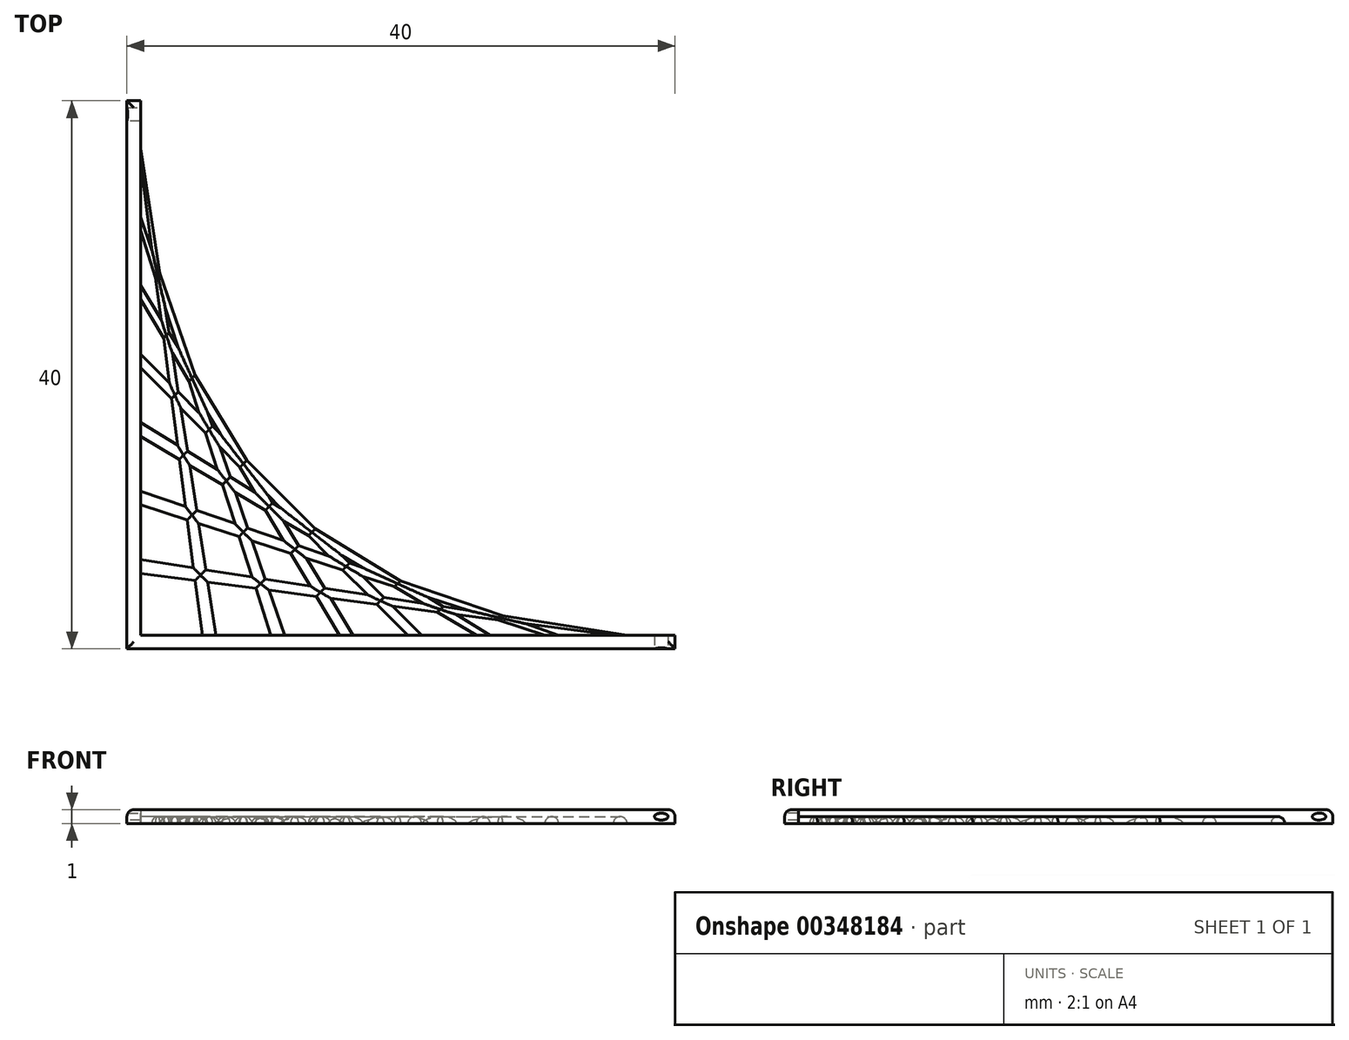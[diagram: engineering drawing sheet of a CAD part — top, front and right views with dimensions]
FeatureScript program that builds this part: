
annotation { "Feature Type Name" : "Feature", "Feature Type Description" : "" }
export const myFeature = defineFeature(function(context is Context, id is Id, definition is map)
    precondition{}
    {
        {
            var Q0;
            Q0=qCreatedBy(makeId("Top.planeOp"),FACE);
            var sketch = newSketch(context, id + "F0", { "sketchPlane" : qUnion([Q0])});
            skLineSegment(sketch, "E0.bottom", {"start": v(0, 0) * mm, "end": v(40, 0) * mm});
            skLineSegment(sketch, "E0.top", {"start": v(0, 1) * mm, "end": v(40, 1) * mm});
            skLineSegment(sketch, "E0.left", {"start": v(0, 0) * mm, "end": v(0, 1) * mm});
            skLineSegment(sketch, "E0.right", {"start": v(40, 0) * mm, "end": v(40, 1) * mm});
            skLineSegment(sketch, "E1.bottom", {"start": v(0, 0) * mm, "end": v(1, 0) * mm});
            skLineSegment(sketch, "E1.top", {"start": v(0, 40) * mm, "end": v(1, 40) * mm});
            skLineSegment(sketch, "E1.left", {"start": v(0, 0) * mm, "end": v(0, 40) * mm});
            skLineSegment(sketch, "E1.right", {"start": v(1, 0) * mm, "end": v(1, 40) * mm});
            skSolve(sketch);
        }
        {
            var Q0;
            Q0 = qSketchRegion(id + "F0", true);
            extrude(context, id + "F1", {"entities" : qUnion([Q0]), "endBound" : BoundingType.SYMMETRIC, "depth" : 1 * mm});
        }
        {
            var Q0;
            Q0=makeQuery(id+"F1.opExtrude","SWEPT_FACE",FACE,{"disambiguationData":[OSD([sQuery(id+"F0.wireOp",EDGE,"E1.right")])]});
            var sketch = newSketch(context, id + "F2", { "sketchPlane" : qUnion([Q0])});
            skArc(sketch, "E2", {"start": v(6.5, -0.5) * mm, "mid": v(6, 0) * mm, "end": v(5.5, -0.5) * mm});
            skLineSegment(sketch, "E3", {"start": v(5.5, -0.5) * mm, "end": v(6.5, -0.5) * mm});
            skArc(sketch, "E4.1.0.0", {"start": v(11.5, -0.5) * mm, "mid": v(11, 0) * mm, "end": v(10.5, -0.5) * mm});
            skArc(sketch, "E4.2.0.0", {"start": v(16.5, -0.5) * mm, "mid": v(16, 0) * mm, "end": v(15.5, -0.5) * mm});
            skArc(sketch, "E4.3.0.0", {"start": v(21.5, -0.5) * mm, "mid": v(21, 0) * mm, "end": v(20.5, -0.5) * mm});
            skArc(sketch, "E4.4.0.0", {"start": v(26.5, -0.5) * mm, "mid": v(26, 0) * mm, "end": v(25.5, -0.5) * mm});
            skLineSegment(sketch, "E4.direction1", {"start": v(5.5, -0.5) * mm, "end": v(10.5, -0.5) * mm, "construction": true});
            skArc(sketch, "E5.0.5.0", {"start": v(31.5, -0.5) * mm, "mid": v(31, 0) * mm, "end": v(30.5, -0.5) * mm});
            skArc(sketch, "E5.0.6.0", {"start": v(36.5, -0.5) * mm, "mid": v(36, 0) * mm, "end": v(35.5, -0.5) * mm});
            skSolve(sketch);
        }
        {
            var Q0;
            Q0=makeQuery(id+"F1.opExtrude","SWEPT_FACE",FACE,{"disambiguationData":[OSD([sQuery(id+"F0.wireOp",EDGE,"E0.top")])]});
            var sketch = newSketch(context, id + "F3", { "sketchPlane" : qUnion([Q0])});
            skArc(sketch, "E6", {"start": v(-5.5, -0.5) * mm, "mid": v(-6, 0) * mm, "end": v(-6.5, -0.5) * mm});
            skLineSegment(sketch, "E7", {"start": v(-5.5, -0.5) * mm, "end": v(-6.5, -0.5) * mm});
            skArc(sketch, "E8.1.0.0", {"start": v(-10.5, -0.5) * mm, "mid": v(-11, 0) * mm, "end": v(-11.5, -0.5) * mm});
            skArc(sketch, "E8.2.0.0", {"start": v(-15.5, -0.5) * mm, "mid": v(-16, 0) * mm, "end": v(-16.5, -0.5) * mm});
            skArc(sketch, "E8.3.0.0", {"start": v(-20.5, -0.5) * mm, "mid": v(-21, 0) * mm, "end": v(-21.5, -0.5) * mm});
            skArc(sketch, "E8.4.0.0", {"start": v(-25.5, -0.5) * mm, "mid": v(-26, 0) * mm, "end": v(-26.5, -0.5) * mm});
            skLineSegment(sketch, "E8.direction1", {"start": v(-6.5, -0.5) * mm, "end": v(-11.5, -0.5) * mm, "construction": true});
            skArc(sketch, "E9.0.5.0", {"start": v(-30.5, -0.5) * mm, "mid": v(-31, 0) * mm, "end": v(-31.5, -0.5) * mm});
            skArc(sketch, "E9.0.6.0", {"start": v(-35.5, -0.5) * mm, "mid": v(-36, 0) * mm, "end": v(-36.5, -0.5) * mm});
            skSolve(sketch);
        }
        {
            var Q1;
            Q1=makeQuery(id+"F2.imprint","IMPRINT",FACE,{"disambiguationData":[TD([[makeQuery(id+"F2.imprint","IMPRINT",EDGE,{"derivedFrom":sQuery(id+"F2.wireOp",EDGE,"E2")}),1.0]])]});
            var Q2;
            {var subQ0=sQuery(id+"F3.wireOp",EDGE,"E9.0.6.0");Q2=makeQuery(id+"F3.imprint","IMPRINT",FACE,{"disambiguationData":[TD([[makeQuery(id+"F3.imprint","IMPRINT",EDGE,{"derivedFrom":subQ0}),1.0]])]});}
            loft(context, id + "F4", {"operationType" : NewBodyOperationType.ADD, "sheetProfilesArray" : [{ "sheetProfileEntities" : qUnion([Q1]) }, { "sheetProfileEntities" : qUnion([Q2]) }]});
        }
        {
            var Q1;
            {var subQ0=sQuery(id+"F2.wireOp",EDGE,"E4.1.0.0");Q1=makeQuery(id+"F2.imprint","IMPRINT",FACE,{"disambiguationData":[TD([[makeQuery(id+"F2.imprint","IMPRINT",EDGE,{"derivedFrom":subQ0}),1.0]])]});}
            var Q2;
            {var subQ0=sQuery(id+"F3.wireOp",EDGE,"E9.0.5.0");Q2=makeQuery(id+"F3.imprint","IMPRINT",FACE,{"disambiguationData":[TD([[makeQuery(id+"F3.imprint","IMPRINT",EDGE,{"derivedFrom":subQ0}),1.0]])]});}
            loft(context, id + "F5", {"operationType" : NewBodyOperationType.ADD, "sheetProfilesArray" : [{ "sheetProfileEntities" : qUnion([Q1]) }, { "sheetProfileEntities" : qUnion([Q2]) }]});
        }
        {
            var Q1;
            {var subQ0=sQuery(id+"F2.wireOp",EDGE,"E4.2.0.0");Q1=makeQuery(id+"F2.imprint","IMPRINT",FACE,{"disambiguationData":[TD([[makeQuery(id+"F2.imprint","IMPRINT",EDGE,{"derivedFrom":subQ0}),1.0]])]});}
            var Q2;
            {var subQ0=sQuery(id+"F3.wireOp",EDGE,"E8.4.0.0");Q2=makeQuery(id+"F3.imprint","IMPRINT",FACE,{"disambiguationData":[TD([[makeQuery(id+"F3.imprint","IMPRINT",EDGE,{"derivedFrom":subQ0}),1.0]])]});}
            loft(context, id + "F6", {"operationType" : NewBodyOperationType.ADD, "sheetProfilesArray" : [{ "sheetProfileEntities" : qUnion([Q1]) }, { "sheetProfileEntities" : qUnion([Q2]) }]});
        }
        {
            var Q1;
            {var subQ0=sQuery(id+"F2.wireOp",EDGE,"E4.3.0.0");Q1=makeQuery(id+"F2.imprint","IMPRINT",FACE,{"disambiguationData":[TD([[makeQuery(id+"F2.imprint","IMPRINT",EDGE,{"derivedFrom":subQ0}),1.0]])]});}
            var Q2;
            {var subQ0=sQuery(id+"F3.wireOp",EDGE,"E8.3.0.0");Q2=makeQuery(id+"F3.imprint","IMPRINT",FACE,{"disambiguationData":[TD([[makeQuery(id+"F3.imprint","IMPRINT",EDGE,{"derivedFrom":subQ0}),1.0]])]});}
            loft(context, id + "F7", {"operationType" : NewBodyOperationType.ADD, "sheetProfilesArray" : [{ "sheetProfileEntities" : qUnion([Q1]) }, { "sheetProfileEntities" : qUnion([Q2]) }]});
        }
        {
            var Q1;
            {var subQ0=sQuery(id+"F2.wireOp",EDGE,"E4.4.0.0");Q1=makeQuery(id+"F2.imprint","IMPRINT",FACE,{"disambiguationData":[TD([[makeQuery(id+"F2.imprint","IMPRINT",EDGE,{"derivedFrom":subQ0}),1.0]])]});}
            var Q2;
            {var subQ0=sQuery(id+"F3.wireOp",EDGE,"E8.2.0.0");Q2=makeQuery(id+"F3.imprint","IMPRINT",FACE,{"disambiguationData":[TD([[makeQuery(id+"F3.imprint","IMPRINT",EDGE,{"derivedFrom":subQ0}),1.0]])]});}
            loft(context, id + "F8", {"operationType" : NewBodyOperationType.ADD, "sheetProfilesArray" : [{ "sheetProfileEntities" : qUnion([Q1]) }, { "sheetProfileEntities" : qUnion([Q2]) }]});
        }
        {
            var Q1;
            {var subQ0=sQuery(id+"F2.wireOp",EDGE,"E5.0.5.0");Q1=makeQuery(id+"F2.imprint","IMPRINT",FACE,{"disambiguationData":[TD([[makeQuery(id+"F2.imprint","IMPRINT",EDGE,{"derivedFrom":subQ0}),1.0]])]});}
            var Q2;
            {var subQ0=sQuery(id+"F3.wireOp",EDGE,"E8.1.0.0");Q2=makeQuery(id+"F3.imprint","IMPRINT",FACE,{"disambiguationData":[TD([[makeQuery(id+"F3.imprint","IMPRINT",EDGE,{"derivedFrom":subQ0}),1.0]])]});}
            loft(context, id + "F9", {"operationType" : NewBodyOperationType.ADD, "sheetProfilesArray" : [{ "sheetProfileEntities" : qUnion([Q1]) }, { "sheetProfileEntities" : qUnion([Q2]) }]});
        }
        {
            var Q1;
            {var subQ0=sQuery(id+"F2.wireOp",EDGE,"E5.0.6.0");Q1=makeQuery(id+"F2.imprint","IMPRINT",FACE,{"disambiguationData":[TD([[makeQuery(id+"F2.imprint","IMPRINT",EDGE,{"derivedFrom":subQ0}),1.0]])]});}
            var Q2;
            Q2=makeQuery(id+"F3.imprint","IMPRINT",FACE,{"disambiguationData":[TD([[makeQuery(id+"F3.imprint","IMPRINT",EDGE,{"derivedFrom":sQuery(id+"F3.wireOp",EDGE,"E6")}),1.0]])]});
            loft(context, id + "F10", {"operationType" : NewBodyOperationType.ADD, "sheetProfilesArray" : [{ "sheetProfileEntities" : qUnion([Q1]) }, { "sheetProfileEntities" : qUnion([Q2]) }]});
        }
        {
            var Q0;
            Q0=makeQuery(id+"F1.opExtrude","SWEPT_FACE",FACE,{"disambiguationData":[OSD([sQuery(id+"F0.wireOp",EDGE,"E1.left")])]});
            var sketch = newSketch(context, id + "F11", { "sketchPlane" : qUnion([Q0])});
            skEllipse(sketch, "E10", {"center": v(-39, 0) * mm, "majorRadius": 0.5 * mm, "minorRadius": 0.25 * mm, "majorAxis": v(1, 0)});
            skSolve(sketch);
        }
        {
            var Q0;
            Q0=makeQuery(id+"F11.imprint","IMPRINT",FACE,{"disambiguationData":[TD([[makeQuery(id+"F11.imprint","IMPRINT",EDGE,{"derivedFrom":sQuery(id+"F11.wireOp",EDGE,"E10")}),1.0]])]});
            var Q1;
            Q1=sQuery(id+"F11.wireOp",EDGE,"E10");
            extrude(context, id + "F12", {"entities" : qUnion([Q0]), "operationType" : NewBodyOperationType.REMOVE, "surfaceEntities" : qUnion([Q1]), "endBound" : BoundingType.THROUGH_ALL, "oppositeDirection" : true, "depth" : 25 * mm});
        }
        {
            var Q0;
            Q0=makeQuery(id+"F1.opExtrude","SWEPT_FACE",FACE,{"disambiguationData":[OSD([sQuery(id+"F0.wireOp",EDGE,"E0.bottom"),sQuery(id+"F0.wireOp",EDGE,"E1.bottom")])]});
            var sketch = newSketch(context, id + "F13", { "sketchPlane" : qUnion([Q0])});
            skEllipse(sketch, "E11", {"center": v(39, 0) * mm, "majorRadius": 0.5 * mm, "minorRadius": 0.25 * mm, "majorAxis": v(1, 0)});
            skSolve(sketch);
        }
        {
            var Q0;
            Q0=makeQuery(id+"F13.imprint","IMPRINT",FACE,{"disambiguationData":[TD([[makeQuery(id+"F13.imprint","IMPRINT",EDGE,{"derivedFrom":sQuery(id+"F13.wireOp",EDGE,"E11")}),1.0]])]});
            extrude(context, id + "F14", {"entities" : qUnion([Q0]), "operationType" : NewBodyOperationType.REMOVE, "endBound" : BoundingType.THROUGH_ALL, "oppositeDirection" : true, "depth" : 25 * mm});
        }
        {
            var Q0;
            Q0=makeQuery(id+"F1.opExtrude","CAP_EDGE",EDGE,{"disambiguationData":[OSD([sQuery(id+"F0.wireOp",EDGE,"E0.bottom"),sQuery(id+"F0.wireOp",EDGE,"E1.bottom")])],"isStart":false});
            var Q1;
            Q1=makeQuery(id+"F1.opExtrude","CAP_EDGE",EDGE,{"disambiguationData":[OSD([sQuery(id+"F0.wireOp",EDGE,"E0.right")])],"isStart":false});
            var Q2;
            Q2=makeQuery(id+"F1.opExtrude","CAP_EDGE",EDGE,{"disambiguationData":[OSD([sQuery(id+"F0.wireOp",EDGE,"E1.left")])],"isStart":false});
            var Q3;
            Q3=makeQuery(id+"F1.opExtrude","CAP_EDGE",EDGE,{"disambiguationData":[OSD([sQuery(id+"F0.wireOp",EDGE,"E1.top")])],"isStart":false});
            fillet(context, id + "F15", {"entities" : qUnion([Q0, Q1, Q2, Q3]), "radius" : .5 * mm, "tangentPropagation" : true, "allowEdgeOverflow" : false});
        }
    });
